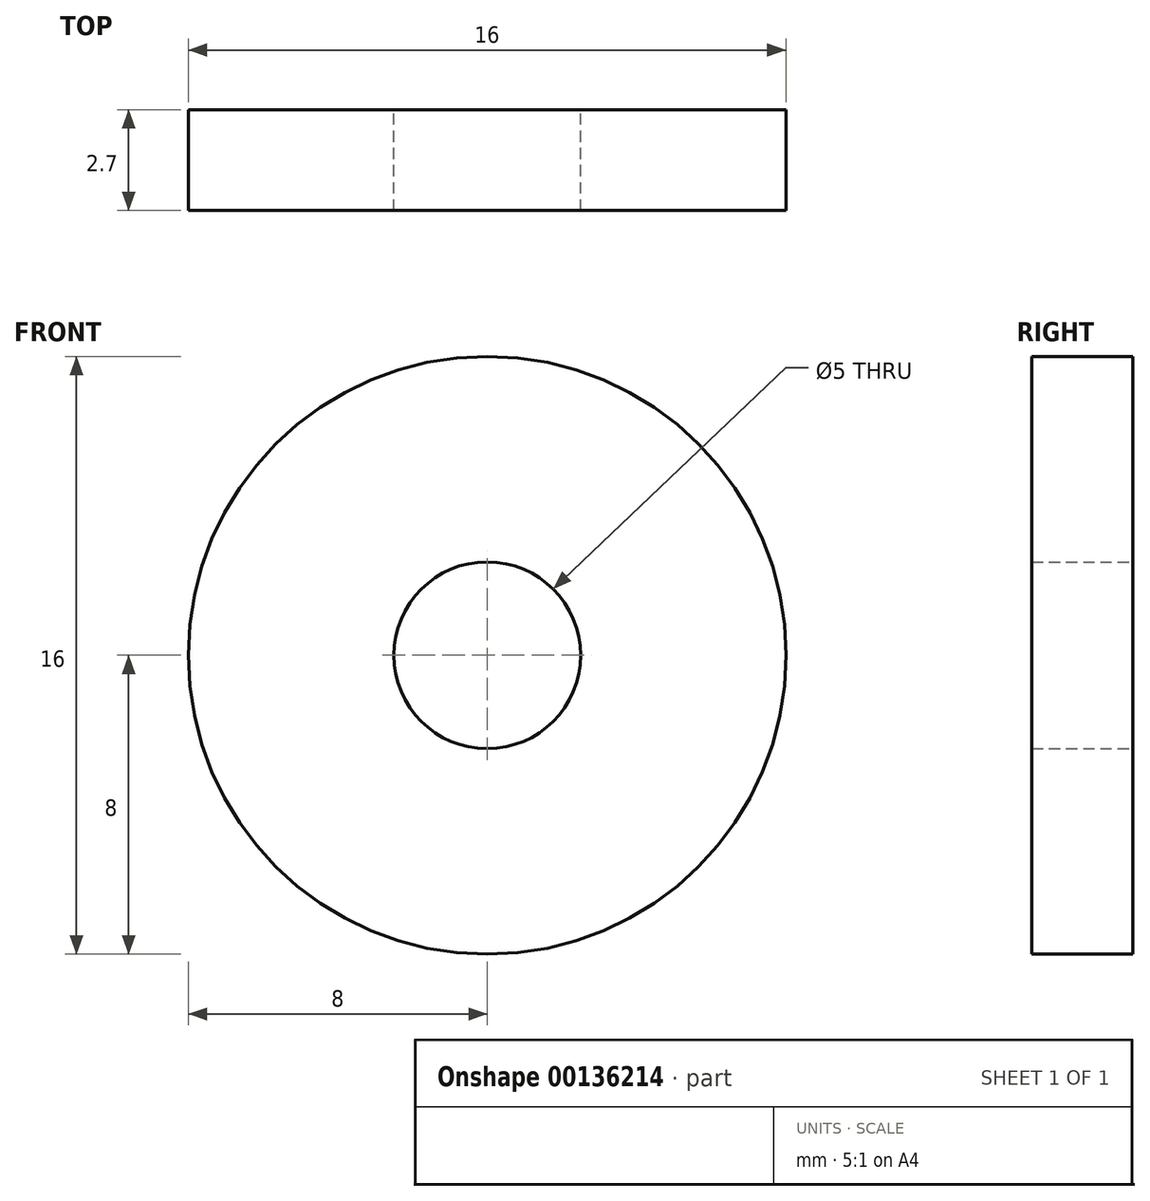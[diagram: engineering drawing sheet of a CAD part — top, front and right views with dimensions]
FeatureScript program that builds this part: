
annotation { "Feature Type Name" : "Feature", "Feature Type Description" : "" }
export const myFeature = defineFeature(function(context is Context, id is Id, definition is map)
    precondition{}
    {
        {
            var Q0;
            Q0=qCreatedBy(makeId("Front.planeOp"),FACE);
            var sketch = newSketch(context, id + "F0", { "sketchPlane" : qUnion([Q0])});
            skCircle(sketch, "E0", {"center": v(0, 0) * mm, "radius": 8 * mm});
            skCircle(sketch, "E1", {"center": v(0, 0) * mm, "radius": 2.5 * mm});
            skSolve(sketch);
        }
        {
            var Q0;
            Q0 = qSketchRegion(id + "F0", true);
            extrude(context, id + "F1", {"entities" : qUnion([Q0]), "depth" : 2.7 * mm});
        }
    });
